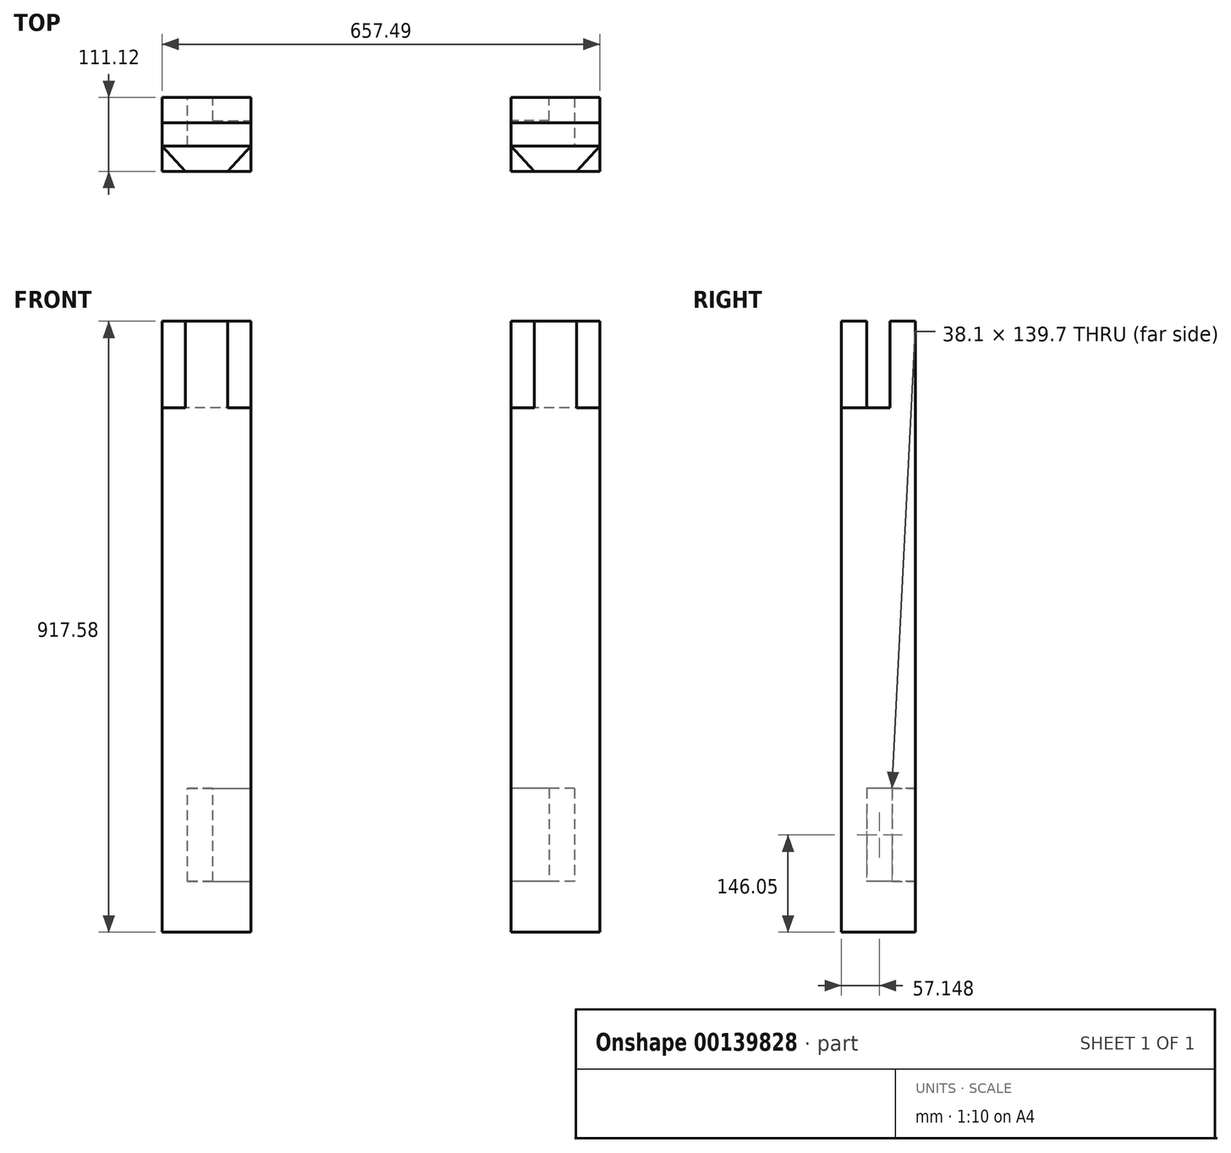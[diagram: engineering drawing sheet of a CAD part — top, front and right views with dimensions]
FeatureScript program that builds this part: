
annotation { "Feature Type Name" : "Feature", "Feature Type Description" : "" }
export const myFeature = defineFeature(function(context is Context, id is Id, definition is map)
    precondition{}
    {
        {
            var Q0;
            Q0=qCreatedBy(makeId("Top.planeOp"),FACE);
            var sketch = newSketch(context, id + "F0", { "sketchPlane" : qUnion([Q0])});
            skLineSegment(sketch, "E0.bottom", {"start": v(-66.67, 55.56) * mm, "end": v(66.67, 55.56) * mm});
            skLineSegment(sketch, "E0.top", {"start": v(-66.67, -55.56) * mm, "end": v(66.67, -55.56) * mm});
            skLineSegment(sketch, "E0.left", {"start": v(-66.67, 55.56) * mm, "end": v(-66.67, -55.56) * mm});
            skLineSegment(sketch, "E0.right", {"start": v(66.68, 55.56) * mm, "end": v(66.68, -55.56) * mm});
            skSolve(sketch);
        }
        {
            var Q0;
            Q0 = qSketchRegion(id + "F0", true);
            extrude(context, id + "F1", {"entities" : qUnion([Q0]), "depth" : 787.4 * mm});
        }
        {
            var Q0;
            Q0=makeQuery(id+"F1.opExtrude","CAP_FACE",FACE,{"disambiguationData":[OSD([sQuery(id+"F0.wireOp",EDGE,"E0.bottom"),sQuery(id+"F0.wireOp",EDGE,"E0.top"),sQuery(id+"F0.wireOp",EDGE,"E0.left"),sQuery(id+"F0.wireOp",EDGE,"E0.right")])],"isStart":false});
            var sketch = newSketch(context, id + "F2", { "sketchPlane" : qUnion([Q0])});
            skLineSegment(sketch, "E1.bottom", {"start": v(-66.67, 55.56) * mm, "end": v(66.68, 55.56) * mm});
            skLineSegment(sketch, "E1.top", {"start": v(-66.67, 17.46) * mm, "end": v(66.68, 17.46) * mm});
            skLineSegment(sketch, "E1.left", {"start": v(-66.67, 55.56) * mm, "end": v(-66.67, 17.46) * mm});
            skLineSegment(sketch, "E1.right", {"start": v(66.68, 55.56) * mm, "end": v(66.68, 17.46) * mm});
            skLineSegment(sketch, "E2", {"start": v(66.68, -17.46) * mm, "end": v(-66.67, -17.46) * mm});
            skLineSegment(sketch, "E3", {"start": v(-66.68, -17.46) * mm, "end": v(-31.75, -55.56) * mm});
            skLineSegment(sketch, "E4", {"start": v(-31.75, -55.56) * mm, "end": v(31.75, -55.56) * mm});
            skLineSegment(sketch, "E5", {"start": v(31.75, -55.56) * mm, "end": v(66.68, -17.46) * mm});
            skSolve(sketch);
        }
        {
            var Q0;
            Q0 = qSketchRegion(id + "F2", true);
            extrude(context, id + "F3", {"entities" : qUnion([Q0]), "operationType" : NewBodyOperationType.ADD, "depth" : 130.17 * mm});
        }
        {
            var Q0;
            Q0=makeQuery(id+"F1.opExtrude","SWEPT_BODY",BODY,{"disambiguationData":[OSD([sQuery(id+"F0.wireOp",EDGE,"E0.bottom"),sQuery(id+"F0.wireOp",EDGE,"E0.top"),sQuery(id+"F0.wireOp",EDGE,"E0.left"),sQuery(id+"F0.wireOp",EDGE,"E0.right")])]});
            transform(context, id + "F4", {"entities" : qUnion([Q0]), "transformType" : TransformType.TRANSLATION_3D, "dx" : 524.14 * mm, "dy" : 0 * mm, "dz" : 0 * mm, "makeCopy" : true});
        }
        {
            var Q0;
            Q0=makeQuery(id+"F3.boolean.opBoolean","MERGE",FACE,{"derivedFrom":[makeQuery(id+"F1.opExtrude","SWEPT_FACE",FACE,{"disambiguationData":[OSD([sQuery(id+"F0.wireOp",EDGE,"E0.right")])]}),makeQuery(id+"F3.opExtrude","SWEPT_FACE",FACE,{"disambiguationData":[OSD([sQuery(id+"F2.wireOp",EDGE,"E1.right")])]})]});
            var sketch = newSketch(context, id + "F5", { "sketchPlane" : qUnion([Q0])});
            skLineSegment(sketch, "E6.bottom", {"start": v(-17.46, 76.2) * mm, "end": v(20.64, 76.2) * mm});
            skLineSegment(sketch, "E6.top", {"start": v(-17.46, 215.9) * mm, "end": v(20.64, 215.9) * mm});
            skLineSegment(sketch, "E6.left", {"start": v(-17.46, 76.2) * mm, "end": v(-17.46, 215.9) * mm});
            skLineSegment(sketch, "E6.right", {"start": v(20.64, 76.2) * mm, "end": v(20.64, 215.9) * mm});
            skSolve(sketch);
        }
        {
            var Q0;
            Q0 = qSketchRegion(id + "F5", true);
            extrude(context, id + "F6", {"entities" : qUnion([Q0]), "operationType" : NewBodyOperationType.REMOVE, "oppositeDirection" : true, "depth" : 95.25 * mm});
        }
        {
            var Q0;
            Q0=makeQuery(id+"F3.boolean.opBoolean","MERGE",FACE,{"derivedFrom":[makeQuery(id+"F1.opExtrude","SWEPT_FACE",FACE,{"disambiguationData":[OSD([sQuery(id+"F0.wireOp",EDGE,"E0.bottom")])]}),makeQuery(id+"F3.opExtrude","SWEPT_FACE",FACE,{"disambiguationData":[OSD([sQuery(id+"F2.wireOp",EDGE,"E1.bottom")])]})]});
            var sketch = newSketch(context, id + "F7", { "sketchPlane" : qUnion([Q0])});
            skLineSegment(sketch, "E7.bottom", {"start": v(-9.53, 76.2) * mm, "end": v(28.57, 76.2) * mm});
            skLineSegment(sketch, "E7.top", {"start": v(-9.53, 215.9) * mm, "end": v(28.57, 215.9) * mm});
            skLineSegment(sketch, "E7.left", {"start": v(-9.53, 76.2) * mm, "end": v(-9.53, 215.9) * mm});
            skLineSegment(sketch, "E7.right", {"start": v(28.57, 76.2) * mm, "end": v(28.57, 215.9) * mm});
            skSolve(sketch);
        }
        {
            var Q0;
            Q0 = qSketchRegion(id + "F7", true);
            extrude(context, id + "F8", {"entities" : qUnion([Q0]), "operationType" : NewBodyOperationType.REMOVE, "endBound" : BoundingType.UP_TO_NEXT, "oppositeDirection" : true, "depth" : 25.4 * mm});
        }
        {
            var Q0;
            Q0=makeQuery(id+"F4.opPattern","COPY",FACE,{"derivedFrom":makeQuery(id+"F3.boolean.opBoolean","MERGE",FACE,{"derivedFrom":[makeQuery(id+"F1.opExtrude","SWEPT_FACE",FACE,{"disambiguationData":[OSD([sQuery(id+"F0.wireOp",EDGE,"E0.bottom")])]}),makeQuery(id+"F3.opExtrude","SWEPT_FACE",FACE,{"disambiguationData":[OSD([sQuery(id+"F2.wireOp",EDGE,"E1.bottom")])]})]}),"instanceName":"1"});
            var sketch = newSketch(context, id + "F9", { "sketchPlane" : qUnion([Q0])});
            skLineSegment(sketch, "E8.bottom", {"start": v(-552.72, 215.9) * mm, "end": v(-514.62, 215.9) * mm});
            skLineSegment(sketch, "E8.top", {"start": v(-552.72, 76.2) * mm, "end": v(-514.62, 76.2) * mm});
            skLineSegment(sketch, "E8.left", {"start": v(-552.72, 215.9) * mm, "end": v(-552.72, 76.2) * mm});
            skLineSegment(sketch, "E8.right", {"start": v(-514.62, 215.9) * mm, "end": v(-514.62, 76.2) * mm});
            skSolve(sketch);
        }
        {
            var Q0;
            Q0=makeQuery(id+"F4.opPattern","COPY",FACE,{"derivedFrom":makeQuery(id+"F3.boolean.opBoolean","MERGE",FACE,{"derivedFrom":[makeQuery(id+"F1.opExtrude","SWEPT_FACE",FACE,{"disambiguationData":[OSD([sQuery(id+"F0.wireOp",EDGE,"E0.left")])]}),makeQuery(id+"F3.opExtrude","SWEPT_FACE",FACE,{"disambiguationData":[OSD([sQuery(id+"F2.wireOp",EDGE,"E1.left")])]})]}),"instanceName":"1"});
            var sketch = newSketch(context, id + "F10", { "sketchPlane" : qUnion([Q0])});
            skLineSegment(sketch, "E9.bottom", {"start": v(-20.64, 215.9) * mm, "end": v(17.46, 215.9) * mm});
            skLineSegment(sketch, "E9.top", {"start": v(-20.64, 76.2) * mm, "end": v(17.46, 76.2) * mm});
            skLineSegment(sketch, "E9.left", {"start": v(-20.64, 215.9) * mm, "end": v(-20.64, 76.2) * mm});
            skLineSegment(sketch, "E9.right", {"start": v(17.46, 215.9) * mm, "end": v(17.46, 76.2) * mm});
            skSolve(sketch);
        }
        {
            var Q0;
            Q0 = qSketchRegion(id + "F10", true);
            extrude(context, id + "F11", {"entities" : qUnion([Q0]), "operationType" : NewBodyOperationType.REMOVE, "oppositeDirection" : true, "depth" : 95.25 * mm});
        }
        {
            var Q0;
            Q0=makeQuery(id+"F9.imprint","IMPRINT",FACE,{"disambiguationData":[TD([[makeQuery(id+"F9.imprint","IMPRINT",EDGE,{"derivedFrom":sQuery(id+"F9.wireOp",EDGE,"E8.bottom")}),-1.0]])]});
            extrude(context, id + "F12", {"entities" : qUnion([Q0]), "operationType" : NewBodyOperationType.REMOVE, "endBound" : BoundingType.UP_TO_NEXT, "oppositeDirection" : true, "depth" : 25.4 * mm});
        }
    });
